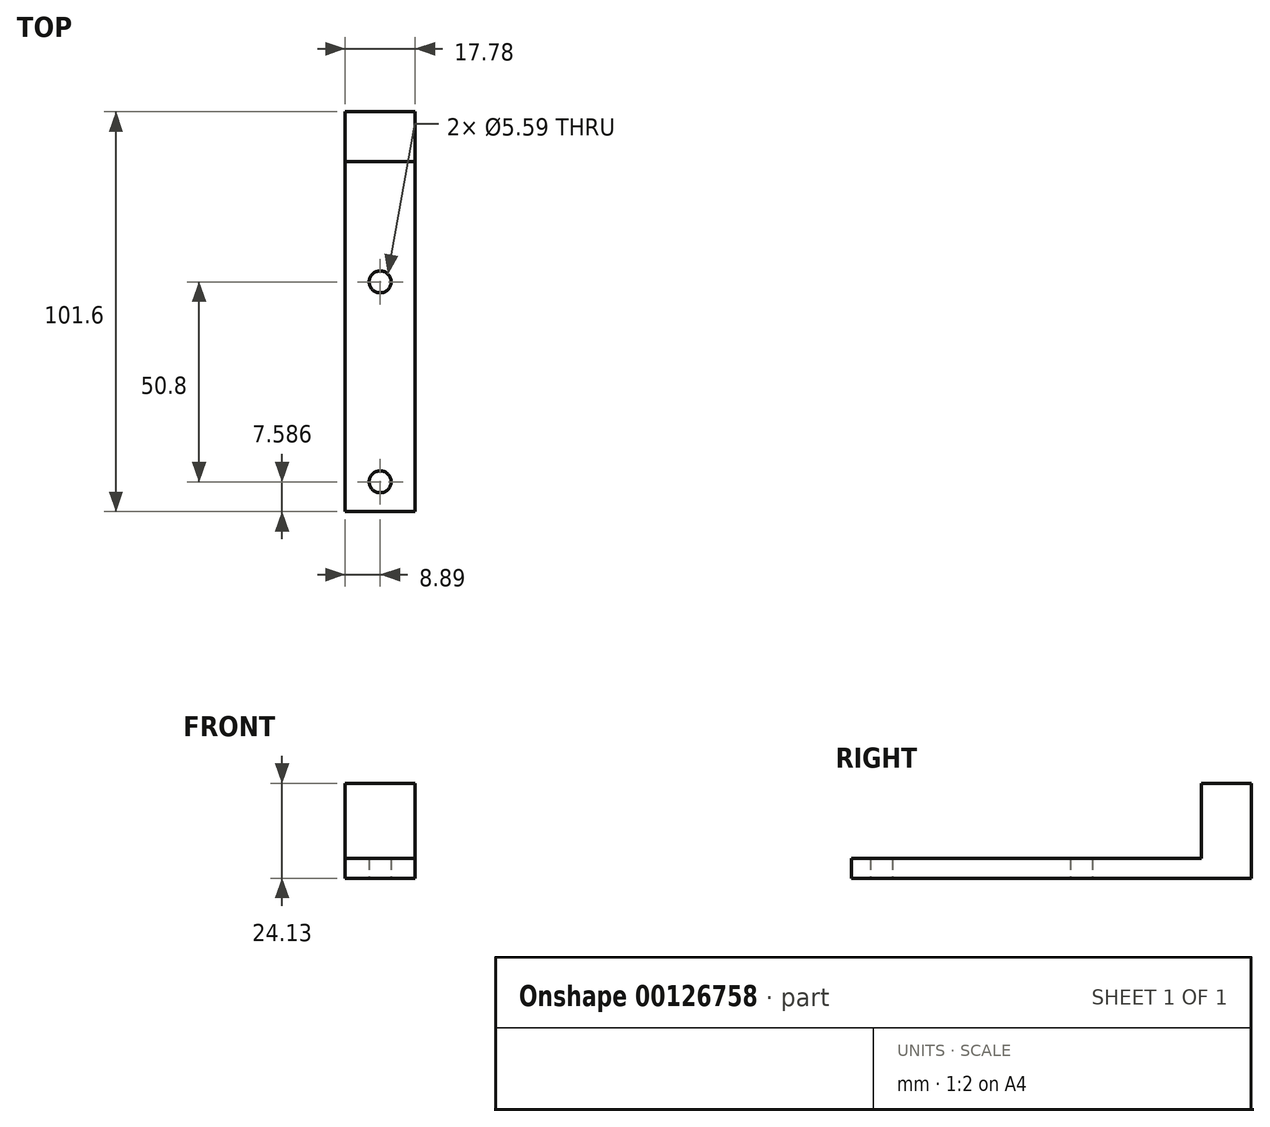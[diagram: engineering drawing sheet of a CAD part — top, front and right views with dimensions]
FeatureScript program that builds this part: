
annotation { "Feature Type Name" : "Feature", "Feature Type Description" : "" }
export const myFeature = defineFeature(function(context is Context, id is Id, definition is map)
    precondition{}
    {
        {
            var Q0;
            Q0=qCreatedBy(makeId("Top.planeOp"),FACE);
            var sketch = newSketch(context, id + "F0", { "sketchPlane" : qUnion([Q0])});
            skLineSegment(sketch, "E0.bottom", {"start": v(-8.9, 63.5) * mm, "end": v(8.9, 63.5) * mm});
            skLineSegment(sketch, "E0.top", {"start": v(-8.89, -38.1) * mm, "end": v(8.9, -38.1) * mm});
            skLineSegment(sketch, "E0.left", {"start": v(-8.9, 63.5) * mm, "end": v(-8.89, -38.1) * mm});
            skLineSegment(sketch, "E0.right", {"start": v(8.9, 63.5) * mm, "end": v(8.9, -38.1) * mm});
            skCircle(sketch, "E1", {"center": v(0, -30.51) * mm, "radius": 2.8 * mm});
            skPoint(sketch, "E1.centerSnap0", {"position": v(0, -38.1) * mm});
            skCircle(sketch, "E2", {"center": v(0, 20.29) * mm, "radius": 2.8 * mm});
            skSolve(sketch);
        }
        {
            var Q0;
            Q0=makeQuery(id+"F0.imprint","IMPRINT",FACE,{"disambiguationData":[TD([[makeQuery(id+"F0.imprint","IMPRINT",EDGE,{"derivedFrom":sQuery(id+"F0.wireOp",EDGE,"E0.bottom")}),-1.0]])]});
            extrude(context, id + "F1", {"entities" : qUnion([Q0]), "depth" : 5.08 * mm});
        }
        {
            var Q0;
            Q0=makeQuery(id+"F1.opExtrude","CAP_FACE",FACE,{"disambiguationData":[OSD([sQuery(id+"F0.wireOp",EDGE,"E0.bottom"),sQuery(id+"F0.wireOp",EDGE,"E0.top"),sQuery(id+"F0.wireOp",EDGE,"E0.left"),sQuery(id+"F0.wireOp",EDGE,"E0.right"),sQuery(id+"F0.wireOp",EDGE,"E1"),sQuery(id+"F0.wireOp",EDGE,"E2")])],"isStart":false});
            var sketch = newSketch(context, id + "F2", { "sketchPlane" : qUnion([Q0])});
            skLineSegment(sketch, "E3", {"start": v(-8.9, 50.8) * mm, "end": v(8.9, 50.8) * mm});
            skSolve(sketch);
        }
        {
            var Q0;
            {var subQ0=sQuery(id+"F2.wireOp",EDGE,"E3");Q0=makeQuery(id+"F2.imprint","IMPRINT",FACE,{"disambiguationData":[TD([[makeQuery(id+"F2.imprint","IMPRINT",EDGE,{"derivedFrom":subQ0}),1.0]])]});}
            extrude(context, id + "F3", {"entities" : qUnion([Q0]), "operationType" : NewBodyOperationType.ADD, "depth" : 19.05 * mm});
        }
    });
